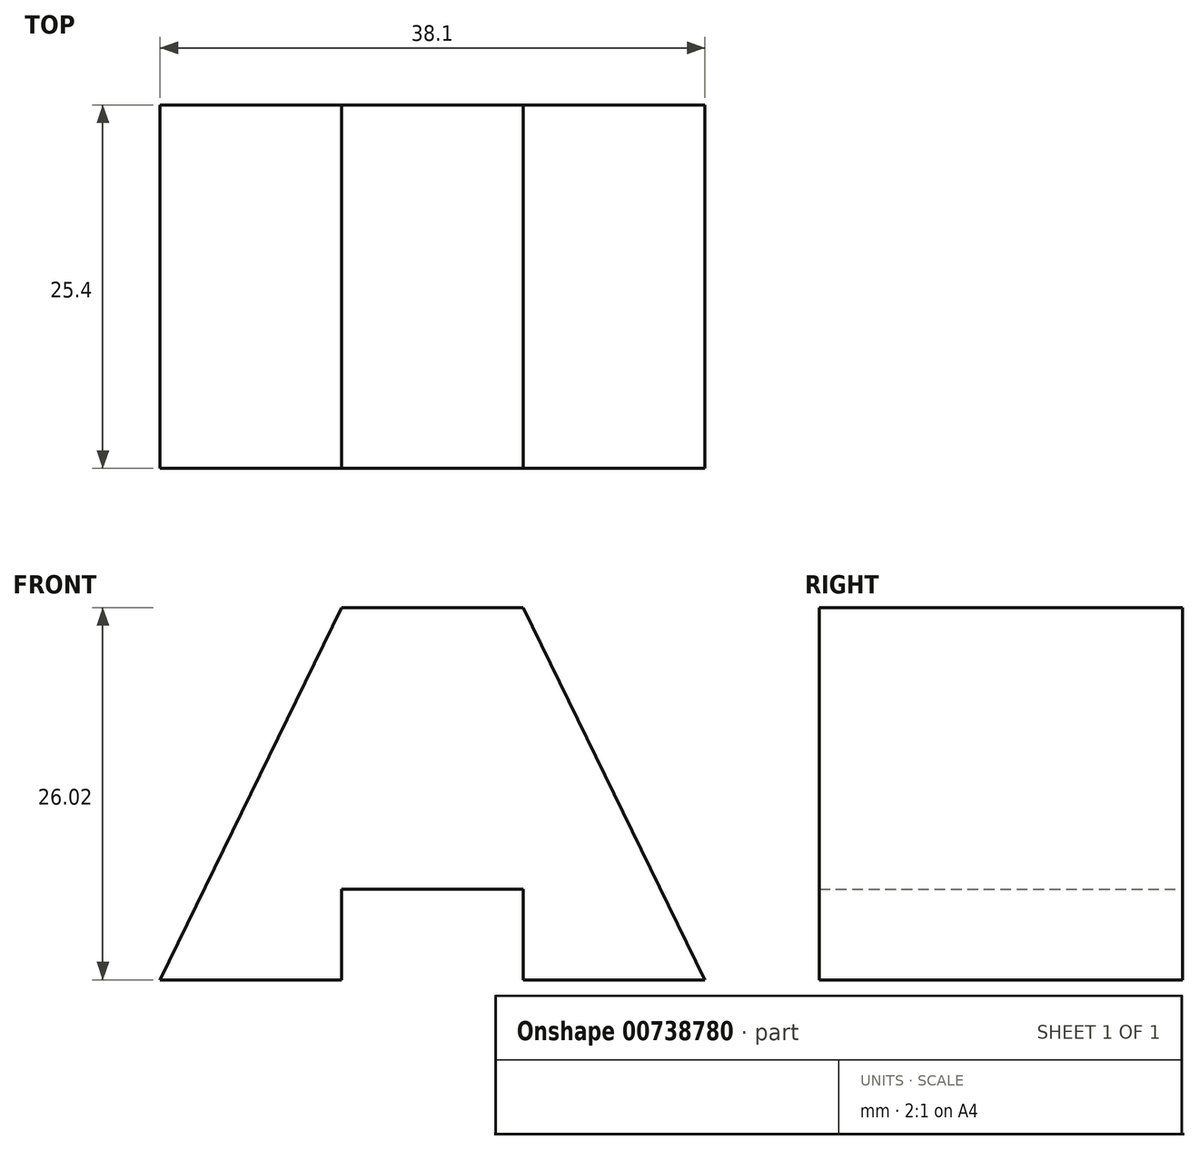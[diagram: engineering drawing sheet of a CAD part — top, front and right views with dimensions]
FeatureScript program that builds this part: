
annotation { "Feature Type Name" : "Feature", "Feature Type Description" : "" }
export const myFeature = defineFeature(function(context is Context, id is Id, definition is map)
    precondition{}
    {
        {
            var Q0;
            Q0=qCreatedBy(makeId("Front.planeOp"),FACE);
            var sketch = newSketch(context, id + "F0", { "sketchPlane" : qUnion([Q0])});
            skLineSegment(sketch, "E0", {"start": v(0, 0) * mm, "end": v(12.69, 26.02) * mm});
            skLineSegment(sketch, "E1", {"start": v(12.69, 26.02) * mm, "end": v(25.39, 26.02) * mm});
            skLineSegment(sketch, "E2", {"start": v(25.39, 26.02) * mm, "end": v(38.1, 0) * mm});
            skLineSegment(sketch, "E3", {"start": v(38.1, 0) * mm, "end": v(25.4, 0) * mm});
            skLineSegment(sketch, "E4", {"start": v(25.4, 0) * mm, "end": v(25.4, 6.35) * mm});
            skLineSegment(sketch, "E5", {"start": v(25.4, 6.35) * mm, "end": v(12.7, 6.35) * mm});
            skLineSegment(sketch, "E6", {"start": v(12.7, 6.35) * mm, "end": v(12.7, 0) * mm});
            skLineSegment(sketch, "E7", {"start": v(12.7, 0) * mm, "end": v(0, 0) * mm});
            skSolve(sketch);
        }
        {
            var Q0;
            Q0 = qSketchRegion(id + "F0", true);
            extrude(context, id + "F1", {"entities" : qUnion([Q0]), "depth" : 25.4 * mm, "offsetDistance" : 25.4 * mm});
        }
    });
